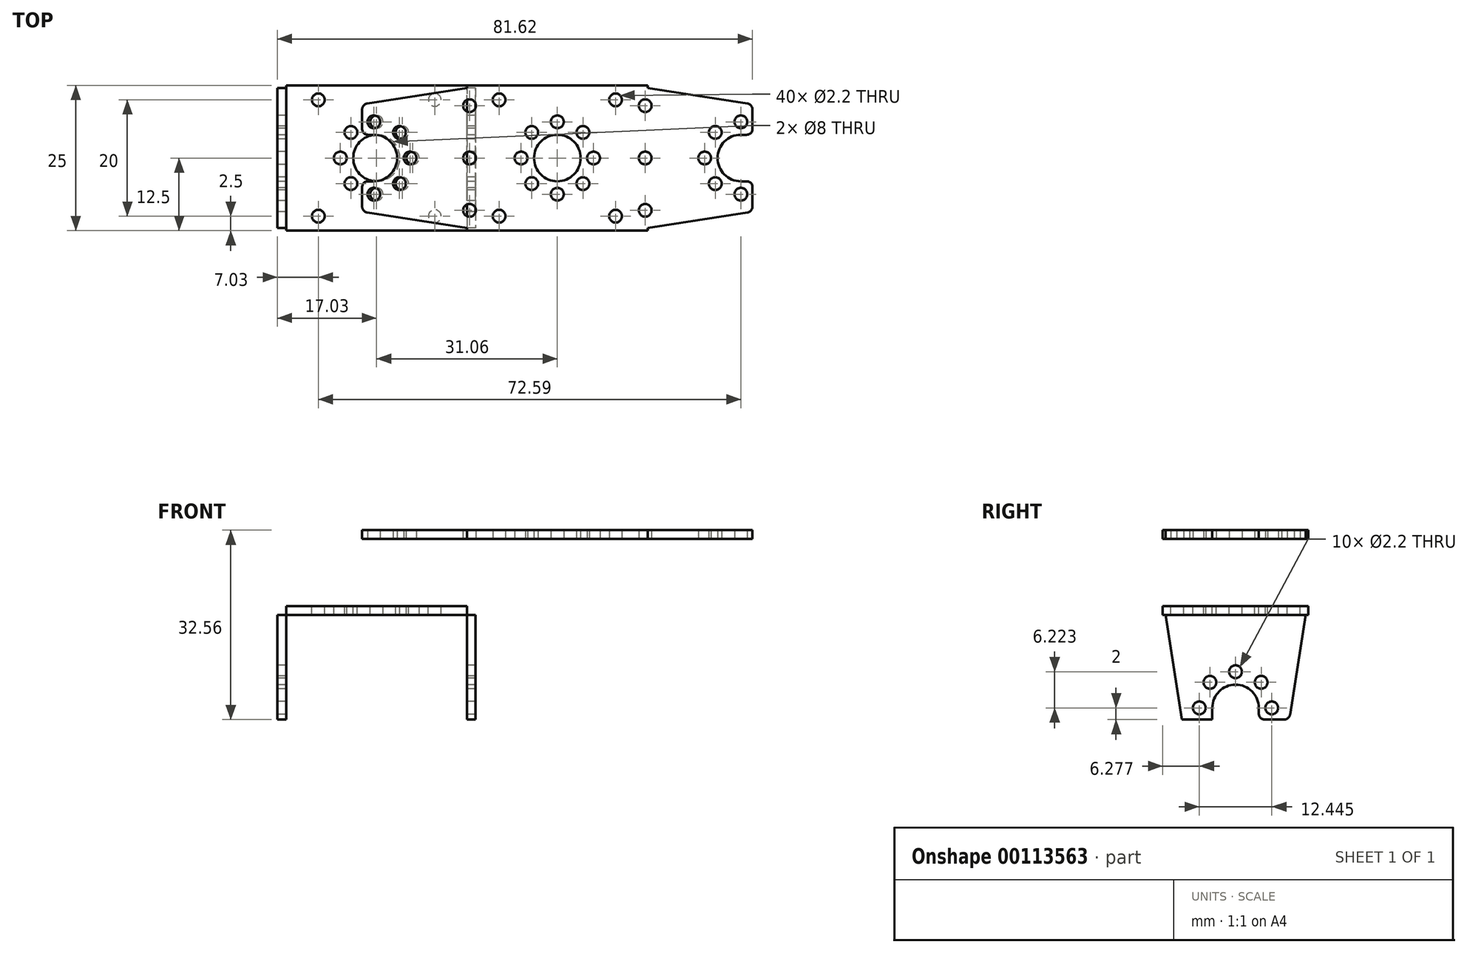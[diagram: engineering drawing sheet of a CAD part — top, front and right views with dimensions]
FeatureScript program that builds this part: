
annotation { "Feature Type Name" : "Feature", "Feature Type Description" : "" }
export const myFeature = defineFeature(function(context is Context, id is Id, definition is map)
    precondition{}
    {
        {
            var Q0;
            Q0=qCreatedBy(makeId("Front.planeOp"),FACE);
            var sketch = newSketch(context, id + "F0", { "sketchPlane" : qUnion([Q0])});
            skLineSegment(sketch, "E0.bottom", {"start": v(0, 0) * mm, "end": v(1.5, 0) * mm});
            skLineSegment(sketch, "E0.top", {"start": v(0, 19.5) * mm, "end": v(34.06, 19.5) * mm});
            skLineSegment(sketch, "E0.left", {"start": v(0, 0) * mm, "end": v(0, 19.5) * mm});
            skLineSegment(sketch, "E0.right", {"start": v(34.06, 0) * mm, "end": v(34.06, 19.5) * mm});
            skLineSegment(sketch, "E1.top", {"start": v(1.5, 18) * mm, "end": v(32.56, 18) * mm});
            skLineSegment(sketch, "E1.left", {"start": v(1.5, 0) * mm, "end": v(1.5, 18) * mm});
            skLineSegment(sketch, "E1.right", {"start": v(32.56, 0) * mm, "end": v(32.56, 18) * mm});
            skLineSegment(sketch, "E2.trimOffspring", {"start": v(32.56, 0) * mm, "end": v(34.06, 0) * mm});
            skSolve(sketch);
        }
        {
            var Q0;
            Q0=qSketchRegion(id+"F0",true);
            extrude(context, id + "F1", {"entities" : qUnion([Q0]), "depth" : 25 * mm});
        }
        {
            var Q0;
            Q0=makeQuery(id+"F1.opExtrude","SWEPT_FACE",FACE,{"disambiguationData":[OSD([sQuery(id+"F0.wireOp",EDGE,"E0.left")])]});
            var sketch = newSketch(context, id + "F2", { "sketchPlane" : qUnion([Q0])});
            skArc(sketch, "E3", {"start": v(16.5, 2) * mm, "mid": v(12.5, 6) * mm, "end": v(8.5, 2) * mm});
            skCircle(sketch, "E4", {"center": v(18.72, 2) * mm, "radius": 1.1 * mm});
            skCircle(sketch, "E5.1.0", {"center": v(16.9, 6.4) * mm, "radius": 1.1 * mm});
            skCircle(sketch, "E5.2.0", {"center": v(12.5, 8.22) * mm, "radius": 1.1 * mm});
            skCircle(sketch, "E5.3.0", {"center": v(8.1, 6.4) * mm, "radius": 1.1 * mm});
            skCircle(sketch, "E5.4.0", {"center": v(6.28, 2) * mm, "radius": 1.1 * mm});
            skLineSegment(sketch, "E6", {"start": v(8.5, 2) * mm, "end": v(8.5, 0) * mm});
            skLineSegment(sketch, "E7", {"start": v(16.5, 2) * mm, "end": v(16.5, 0) * mm});
            skLineSegment(sketch, "E8", {"start": v(8.5, 0) * mm, "end": v(16.5, 0) * mm});
            skLineSegment(sketch, "E9", {"start": v(12.5, 19.5) * mm, "end": v(12.5, 0) * mm, "construction": true});
            skPoint(sketch, "E10", {"position": v(12.5, 0) * mm});
            skLineSegment(sketch, "E11", {"start": v(3.28, 0) * mm, "end": v(0.47, 18) * mm});
            skLineSegment(sketch, "E12", {"start": v(3.28, 0) * mm, "end": v(0, 0) * mm});
            skLineSegment(sketch, "E13", {"start": v(0, 0) * mm, "end": v(0, 18) * mm});
            skLineSegment(sketch, "E14.MirrorCS", {"start": v(25, 0) * mm, "end": v(25, 18) * mm});
            skLineSegment(sketch, "E15.MirrorCS", {"start": v(21.72, 0) * mm, "end": v(24.53, 18) * mm});
            skLineSegment(sketch, "E16.MirrorCS", {"start": v(21.72, 0) * mm, "end": v(25, 0) * mm});
            skLineSegment(sketch, "E17", {"start": v(0, 18) * mm, "end": v(0.47, 18) * mm});
            skPoint(sketch, "E18.orphan", {"position": v(0, 21) * mm});
            skLineSegment(sketch, "E19.MirrorCS", {"start": v(25, 18) * mm, "end": v(24.53, 18) * mm});
            skPoint(sketch, "E20.orphan", {"position": v(25, 21) * mm});
            skSolve(sketch);
        }
        {
            var Q0;
            Q0=qSketchRegion(id+"F2",true);
            extrude(context, id + "F3", {"entities" : qUnion([Q0]), "operationType" : NewBodyOperationType.REMOVE, "endBound" : BoundingType.THROUGH_ALL, "oppositeDirection" : true, "depth" : 25 * mm});
        }
        {
            var Q0;
            Q0=makeQuery(id+"F1.opExtrude","SWEPT_FACE",FACE,{"disambiguationData":[OSD([sQuery(id+"F0.wireOp",EDGE,"E0.top")])]});
            var sketch = newSketch(context, id + "F4", { "sketchPlane" : qUnion([Q0])});
            skLineSegment(sketch, "E21", {"start": v(17.03, -1.64) * mm, "end": v(17.03, -24.77) * mm, "construction": true});
            skLineSegment(sketch, "E22", {"start": v(0, -12.5) * mm, "end": v(34.06, -12.5) * mm, "construction": true});
            skCircle(sketch, "E23", {"center": v(7.03, -2.5) * mm, "radius": 1.1 * mm});
            skCircle(sketch, "E24.MirrorC", {"center": v(27.03, -2.5) * mm, "radius": 1.1 * mm});
            skCircle(sketch, "E25.MirrorC", {"center": v(7.03, -22.5) * mm, "radius": 1.1 * mm});
            skCircle(sketch, "E26.MirrorC", {"center": v(27.03, -22.5) * mm, "radius": 1.1 * mm});
            skCircle(sketch, "E27", {"center": v(17.03, -12.5) * mm, "radius": 4 * mm});
            skLineSegment(sketch, "E28.bottom", {"start": v(21.43, -16.9) * mm, "end": v(12.63, -16.9) * mm, "construction": true});
            skLineSegment(sketch, "E28.top", {"start": v(21.43, -8.1) * mm, "end": v(12.63, -8.1) * mm, "construction": true});
            skLineSegment(sketch, "E28.left", {"start": v(21.43, -16.9) * mm, "end": v(21.43, -8.1) * mm, "construction": true});
            skLineSegment(sketch, "E28.right", {"start": v(12.63, -16.9) * mm, "end": v(12.63, -8.1) * mm, "construction": true});
            skCircle(sketch, "E29", {"center": v(12.63, -8.1) * mm, "radius": 1.1 * mm});
            skCircle(sketch, "E30.1.0", {"center": v(10.8, -12.5) * mm, "radius": 1.1 * mm});
            skCircle(sketch, "E30.2.0", {"center": v(12.63, -16.9) * mm, "radius": 1.1 * mm});
            skCircle(sketch, "E30.3.0", {"center": v(17.03, -18.72) * mm, "radius": 1.1 * mm});
            skCircle(sketch, "E31.1.4.0", {"center": v(21.43, -16.9) * mm, "radius": 1.1 * mm});
            skCircle(sketch, "E31.1.5.0", {"center": v(23.25, -12.5) * mm, "radius": 1.1 * mm});
            skCircle(sketch, "E31.1.6.0", {"center": v(21.43, -8.1) * mm, "radius": 1.1 * mm});
            skCircle(sketch, "E31.1.7.0", {"center": v(17.03, -6.28) * mm, "radius": 1.1 * mm});
            skPoint(sketch, "E32", {"position": v(17.03, -24.77) * mm});
            skPoint(sketch, "E33", {"position": v(17.03, 0) * mm});
            skPoint(sketch, "E34", {"position": v(17.03, -25) * mm});
            skSolve(sketch);
        }
        {
            var Q0;
            Q0=qSketchRegion(id+"F4",true);
            extrude(context, id + "F5", {"entities" : qUnion([Q0]), "operationType" : NewBodyOperationType.REMOVE, "endBound" : BoundingType.UP_TO_NEXT, "oppositeDirection" : true, "depth" : 25 * mm});
        }
        {
            var Q0;
            Q0=makeQuery(id+"F3.boolean.opBoolean","COPY",EDGE,{"disambiguationData":[OD(0.0)],"derivedFrom":makeQuery(id+"F3.opExtrude","SWEPT_EDGE",EDGE,{"disambiguationData":[OSD([sQuery(id+"F0.wireOp",EDGE,"E0.bottom"),sQuery(id+"F0.wireOp",EDGE,"E0.left"),sQuery(id+"F2.wireOp",EDGE,"E11"),sQuery(id+"F2.wireOp",EDGE,"E12")])]})});
            var Q1;
            Q1=makeQuery(id+"F3.boolean.opBoolean","COPY",EDGE,{"disambiguationData":[OD(0.0)],"derivedFrom":makeQuery(id+"F3.opExtrude","SWEPT_EDGE",EDGE,{"disambiguationData":[OSD([sQuery(id+"F0.wireOp",EDGE,"E0.bottom"),sQuery(id+"F0.wireOp",EDGE,"E0.left"),sQuery(id+"F2.wireOp",EDGE,"E6"),sQuery(id+"F2.wireOp",EDGE,"E8")])]})});
            var Q2;
            Q2=makeQuery(id+"F3.boolean.opBoolean","COPY",EDGE,{"disambiguationData":[OD(0.0)],"derivedFrom":makeQuery(id+"F3.opExtrude","SWEPT_EDGE",EDGE,{"disambiguationData":[OSD([sQuery(id+"F0.wireOp",EDGE,"E0.bottom"),sQuery(id+"F0.wireOp",EDGE,"E0.left"),sQuery(id+"F2.wireOp",EDGE,"E7"),sQuery(id+"F2.wireOp",EDGE,"E8")])]})});
            var Q3;
            Q3=makeQuery(id+"F3.boolean.opBoolean","COPY",EDGE,{"disambiguationData":[OD(0.0)],"derivedFrom":makeQuery(id+"F3.opExtrude","SWEPT_EDGE",EDGE,{"disambiguationData":[OSD([sQuery(id+"F0.wireOp",EDGE,"E0.bottom"),sQuery(id+"F0.wireOp",EDGE,"E0.left"),sQuery(id+"F2.wireOp",EDGE,"E15.MirrorCS"),sQuery(id+"F2.wireOp",EDGE,"E16.MirrorCS")])]})});
            var Q4;
            Q4=makeQuery(id+"F3.boolean.opBoolean","COPY",EDGE,{"disambiguationData":[OD(1.0)],"derivedFrom":makeQuery(id+"F3.opExtrude","SWEPT_EDGE",EDGE,{"disambiguationData":[OSD([sQuery(id+"F0.wireOp",EDGE,"E0.bottom"),sQuery(id+"F0.wireOp",EDGE,"E0.left"),sQuery(id+"F2.wireOp",EDGE,"E11"),sQuery(id+"F2.wireOp",EDGE,"E12")])]})});
            var Q5;
            Q5=makeQuery(id+"F3.boolean.opBoolean","COPY",EDGE,{"disambiguationData":[OD(1.0)],"derivedFrom":makeQuery(id+"F3.opExtrude","SWEPT_EDGE",EDGE,{"disambiguationData":[OSD([sQuery(id+"F0.wireOp",EDGE,"E0.bottom"),sQuery(id+"F0.wireOp",EDGE,"E0.left"),sQuery(id+"F2.wireOp",EDGE,"E6"),sQuery(id+"F2.wireOp",EDGE,"E8")])]})});
            var Q6;
            Q6=makeQuery(id+"F3.boolean.opBoolean","COPY",EDGE,{"disambiguationData":[OD(1.0)],"derivedFrom":makeQuery(id+"F3.opExtrude","SWEPT_EDGE",EDGE,{"disambiguationData":[OSD([sQuery(id+"F0.wireOp",EDGE,"E0.bottom"),sQuery(id+"F0.wireOp",EDGE,"E0.left"),sQuery(id+"F2.wireOp",EDGE,"E7"),sQuery(id+"F2.wireOp",EDGE,"E8")])]})});
            var Q7;
            Q7=makeQuery(id+"F3.boolean.opBoolean","COPY",EDGE,{"disambiguationData":[OD(1.0)],"derivedFrom":makeQuery(id+"F3.opExtrude","SWEPT_EDGE",EDGE,{"disambiguationData":[OSD([sQuery(id+"F0.wireOp",EDGE,"E0.bottom"),sQuery(id+"F0.wireOp",EDGE,"E0.left"),sQuery(id+"F2.wireOp",EDGE,"E15.MirrorCS"),sQuery(id+"F2.wireOp",EDGE,"E16.MirrorCS")])]})});
            fillet(context, id + "F6", {"entities" : qUnion([Q0, Q1, Q2, Q3, Q4, Q5, Q6, Q7]), "radius" : 1 * mm, "tangentPropagation" : true, "allowEdgeOverflow" : false});
        }
        {
            var Q0;
            Q0=makeQuery(id+"F1.opExtrude","CAP_FACE",FACE,{"disambiguationData":[OSD([sQuery(id+"F0.wireOp",EDGE,"E0.bottom"),sQuery(id+"F0.wireOp",EDGE,"E0.top"),sQuery(id+"F0.wireOp",EDGE,"E0.left"),sQuery(id+"F0.wireOp",EDGE,"E0.right"),sQuery(id+"F0.wireOp",EDGE,"E1.top"),sQuery(id+"F0.wireOp",EDGE,"E1.left"),sQuery(id+"F0.wireOp",EDGE,"E1.right"),sQuery(id+"F0.wireOp",EDGE,"E2.trimOffspring")])],"isStart":false});
            var sketch = newSketch(context, id + "F7", { "sketchPlane" : qUnion([Q0])});
            skLineSegment(sketch, "E35.bottom", {"start": v(0, 19.5) * mm, "end": v(1.5, 19.5) * mm});
            skLineSegment(sketch, "E35.top", {"start": v(0, 18) * mm, "end": v(1.5, 18) * mm});
            skLineSegment(sketch, "E35.left", {"start": v(0, 19.5) * mm, "end": v(0, 18) * mm});
            skLineSegment(sketch, "E35.right", {"start": v(1.5, 19.5) * mm, "end": v(1.5, 18) * mm});
            skLineSegment(sketch, "E36", {"start": v(17.03, 19.5) * mm, "end": v(17.03, 18) * mm, "construction": true});
            skLineSegment(sketch, "E37.MirrorCS", {"start": v(34.06, 19.5) * mm, "end": v(32.56, 19.5) * mm});
            skLineSegment(sketch, "E38.MirrorCS", {"start": v(32.56, 19.5) * mm, "end": v(32.56, 18) * mm});
            skLineSegment(sketch, "E39.MirrorCS", {"start": v(34.06, 19.5) * mm, "end": v(34.06, 18) * mm});
            skLineSegment(sketch, "E40.MirrorCS", {"start": v(34.06, 18) * mm, "end": v(32.56, 18) * mm});
            skSolve(sketch);
        }
        {
            var Q0;
            Q0 = qSketchRegion(id + "F7", true);
            extrude(context, id + "F8", {"entities" : qUnion([Q0]), "operationType" : NewBodyOperationType.REMOVE, "endBound" : BoundingType.THROUGH_ALL, "oppositeDirection" : true, "depth" : 25 * mm});
        }
        {
            var Q0;
            Q0=makeQuery(id+"F8.boolean.opBoolean","SPLIT",BODY,{"disambiguationData":[OD(0.0)],"derivedFrom":makeQuery(id+"F1.opExtrude","SWEPT_BODY",BODY,{"disambiguationData":[OSD([sQuery(id+"F0.wireOp",EDGE,"E0.bottom"),sQuery(id+"F0.wireOp",EDGE,"E0.top"),sQuery(id+"F0.wireOp",EDGE,"E0.left"),sQuery(id+"F0.wireOp",EDGE,"E0.right"),sQuery(id+"F0.wireOp",EDGE,"E1.top"),sQuery(id+"F0.wireOp",EDGE,"E1.left"),sQuery(id+"F0.wireOp",EDGE,"E1.right"),sQuery(id+"F0.wireOp",EDGE,"E2.trimOffspring")])]})});
            var Q1;
            {var subQ0=sQuery(id+"F0.wireOp",EDGE,"E1.top");Q1=makeQuery(id+"F8.boolean.opBoolean","MERGE",EDGE,{"disambiguationData":[OD(0.0)],"derivedFrom":[makeQuery(id+"F1.opExtrude","SWEPT_EDGE",EDGE,{"disambiguationData":[OSD([subQ0,sQuery(id+"F0.wireOp",EDGE,"E1.left")])]}),makeQuery(id+"F8.opExtrude","SWEPT_EDGE",EDGE,{"disambiguationData":[OSD([sQuery(id+"F0.wireOp",EDGE,"E0.left"),subQ0,sQuery(id+"F2.wireOp",EDGE,"E14.MirrorCS"),sQuery(id+"F2.wireOp",EDGE,"E19.MirrorCS"),sQuery(id+"F7.wireOp",EDGE,"E35.top"),sQuery(id+"F7.wireOp",EDGE,"E35.right")])]})]});}
            transform(context, id + "F9", {"entities" : qUnion([Q0]), "transformType" : TransformType.ROTATION, "transformAxis" : qUnion([Q1]), "angle" : 90 * degree, "makeCopy" : false});
        }
        {
            var Q0;
            Q0=makeQuery(id+"F8.boolean.opBoolean","SPLIT",BODY,{"disambiguationData":[OD(1.0)],"derivedFrom":makeQuery(id+"F1.opExtrude","SWEPT_BODY",BODY,{"disambiguationData":[OSD([sQuery(id+"F0.wireOp",EDGE,"E0.bottom"),sQuery(id+"F0.wireOp",EDGE,"E0.top"),sQuery(id+"F0.wireOp",EDGE,"E0.left"),sQuery(id+"F0.wireOp",EDGE,"E0.right"),sQuery(id+"F0.wireOp",EDGE,"E1.top"),sQuery(id+"F0.wireOp",EDGE,"E1.left"),sQuery(id+"F0.wireOp",EDGE,"E1.right"),sQuery(id+"F0.wireOp",EDGE,"E2.trimOffspring")])]})});
            var Q1;
            {var subQ0=sQuery(id+"F0.wireOp",EDGE,"E1.top");Q1=makeQuery(id+"F8.boolean.opBoolean","MERGE",EDGE,{"disambiguationData":[OD(0.0)],"derivedFrom":[makeQuery(id+"F1.opExtrude","SWEPT_EDGE",EDGE,{"disambiguationData":[OSD([subQ0,sQuery(id+"F0.wireOp",EDGE,"E1.right")])]}),makeQuery(id+"F8.opExtrude","SWEPT_EDGE",EDGE,{"disambiguationData":[OSD([sQuery(id+"F0.wireOp",EDGE,"E0.left"),subQ0,sQuery(id+"F2.wireOp",EDGE,"E14.MirrorCS"),sQuery(id+"F2.wireOp",EDGE,"E19.MirrorCS"),sQuery(id+"F7.wireOp",EDGE,"E38.MirrorCS"),sQuery(id+"F7.wireOp",EDGE,"E40.MirrorCS")])]})]});}
            transform(context, id + "F10", {"entities" : qUnion([Q0]), "transformType" : TransformType.ROTATION, "transformAxis" : qUnion([Q1]), "angle" : 270 * degree, "makeCopy" : false});
        }
        {
            var Q0;
            Q0=qCreatedBy(makeId("Top.planeOp"),FACE);
            var sketch = newSketch(context, id + "F11", { "sketchPlane" : qUnion([Q0])});
            skCircle(sketch, "E41.0", {"center": v(48.56, -6.28) * mm, "radius": 1.1 * mm});
            skCircle(sketch, "E42.0", {"center": v(44.16, -8.1) * mm, "radius": 1.1 * mm});
            skCircle(sketch, "E43.0", {"center": v(42.34, -12.5) * mm, "radius": 1.1 * mm});
            skCircle(sketch, "E44.0", {"center": v(44.16, -16.9) * mm, "radius": 1.1 * mm});
            skCircle(sketch, "E45.0", {"center": v(48.56, -18.72) * mm, "radius": 1.1 * mm});
            skCircle(sketch, "E46.0", {"center": v(23.25, -12.5) * mm, "radius": 1.1 * mm});
            skCircle(sketch, "E46.1", {"center": v(12.63, -8.1) * mm, "radius": 1.1 * mm});
            skCircle(sketch, "E46.2", {"center": v(10.8, -12.5) * mm, "radius": 1.1 * mm});
            skCircle(sketch, "E46.3", {"center": v(12.63, -16.9) * mm, "radius": 1.1 * mm});
            skCircle(sketch, "E46.4", {"center": v(17.03, -18.72) * mm, "radius": 1.1 * mm});
            skCircle(sketch, "E46.5", {"center": v(17.03, -12.5) * mm, "radius": 4 * mm});
            skCircle(sketch, "E46.6", {"center": v(21.43, -8.1) * mm, "radius": 1.1 * mm});
            skCircle(sketch, "E46.7", {"center": v(21.43, -16.9) * mm, "radius": 1.1 * mm});
            skCircle(sketch, "E46.8", {"center": v(17.03, -6.28) * mm, "radius": 1.1 * mm});
            skCircle(sketch, "E46.9", {"center": v(10.8, -12.5) * mm, "radius": 1.1 * mm});
            skCircle(sketch, "E46.10", {"center": v(17.03, -12.5) * mm, "radius": 4 * mm});
            skCircle(sketch, "E46.11", {"center": v(23.25, -12.5) * mm, "radius": 1.1 * mm});
            skCircle(sketch, "E46.12", {"center": v(21.43, -8.1) * mm, "radius": 1.1 * mm});
            skCircle(sketch, "E46.13", {"center": v(21.43, -16.9) * mm, "radius": 1.1 * mm});
            skCircle(sketch, "E46.14", {"center": v(17.03, -18.72) * mm, "radius": 1.1 * mm});
            skCircle(sketch, "E46.15", {"center": v(12.63, -16.9) * mm, "radius": 1.1 * mm});
            skCircle(sketch, "E46.16", {"center": v(12.63, -8.1) * mm, "radius": 1.1 * mm});
            skCircle(sketch, "E46.17", {"center": v(17.03, -6.28) * mm, "radius": 1.1 * mm});
            skArc(sketch, "E47.0", {"start": v(-15.5, -8.5) * mm, "mid": v(-16.2, -8.2) * mm, "end": v(-16.5, -7.5) * mm});
            skCircle(sketch, "E47.1", {"center": v(-14.5, -18.72) * mm, "radius": 1.1 * mm});
            skCircle(sketch, "E47.2", {"center": v(-8.28, -12.5) * mm, "radius": 1.1 * mm});
            skArc(sketch, "E47.3", {"start": v(-16.5, -17.5) * mm, "mid": v(-16.2, -16.8) * mm, "end": v(-15.5, -16.5) * mm});
            skArc(sketch, "E47.4", {"start": v(-14.5, -16.5) * mm, "mid": v(-10.5, -12.5) * mm, "end": v(-14.5, -8.5) * mm});
            skCircle(sketch, "E47.5", {"center": v(-10.1, -16.9) * mm, "radius": 1.1 * mm});
            skCircle(sketch, "E47.6", {"center": v(-14.5, -6.28) * mm, "radius": 1.1 * mm});
            skCircle(sketch, "E47.7", {"center": v(-10.1, -8.1) * mm, "radius": 1.1 * mm});
            skArc(sketch, "E47.8", {"start": v(-16.5, -7.5) * mm, "mid": v(-16.2, -8.2) * mm, "end": v(-15.5, -8.5) * mm});
            skLineSegment(sketch, "E47.9", {"start": v(-14.5, -8.5) * mm, "end": v(-15.5, -8.5) * mm});
            skArc(sketch, "E47.10", {"start": v(-14.5, -16.5) * mm, "mid": v(-10.5, -12.5) * mm, "end": v(-14.5, -8.5) * mm});
            skCircle(sketch, "E47.11", {"center": v(-10.1, -16.9) * mm, "radius": 1.1 * mm});
            skLineSegment(sketch, "E47.12", {"start": v(-14.5, -16.5) * mm, "end": v(-15.5, -16.5) * mm});
            skLineSegment(sketch, "E47.13", {"start": v(-16.5, -7.5) * mm, "end": v(-16.5, -4.13) * mm});
            skLineSegment(sketch, "E47.15", {"start": v(-14.5, -16.5) * mm, "end": v(-15.5, -16.5) * mm});
            skLineSegment(sketch, "E47.18", {"start": v(-16.5, -7.5) * mm, "end": v(-16.5, -4.13) * mm});
            skCircle(sketch, "E47.19", {"center": v(-14.5, -18.72) * mm, "radius": 1.1 * mm});
            skCircle(sketch, "E47.20", {"center": v(-8.28, -12.5) * mm, "radius": 1.1 * mm});
            skCircle(sketch, "E47.21", {"center": v(-10.1, -8.1) * mm, "radius": 1.1 * mm});
            skCircle(sketch, "E47.22", {"center": v(-14.5, -6.28) * mm, "radius": 1.1 * mm});
            skArc(sketch, "E47.25", {"start": v(-15.5, -16.5) * mm, "mid": v(-16.2, -16.8) * mm, "end": v(-16.5, -17.5) * mm});
            skLineSegment(sketch, "E47.26", {"start": v(-14.5, -8.5) * mm, "end": v(-15.5, -8.5) * mm});
            skLineSegment(sketch, "E48.0", {"start": v(-16.5, -20.87) * mm, "end": v(-16.5, -17.5) * mm});
            skArc(sketch, "E49.0", {"start": v(-15.65, -21.85) * mm, "mid": v(-16.26, -21.52) * mm, "end": v(-16.5, -20.87) * mm});
            skLineSegment(sketch, "E50.0", {"start": v(-15.65, -21.85) * mm, "end": v(1.5, -24.53) * mm});
            skLineSegment(sketch, "E51.0", {"start": v(-15.65, -3.15) * mm, "end": v(1.5, -0.47) * mm});
            skArc(sketch, "E52.0", {"start": v(-16.5, -4.13) * mm, "mid": v(-16.26, -3.48) * mm, "end": v(-15.65, -3.15) * mm});
            skCircle(sketch, "E53.0", {"center": v(7.03, -22.5) * mm, "radius": 1.1 * mm});
            skCircle(sketch, "E54.0", {"center": v(27.03, -22.5) * mm, "radius": 1.1 * mm});
            skCircle(sketch, "E55.0", {"center": v(27.03, -2.5) * mm, "radius": 1.1 * mm});
            skCircle(sketch, "E56.0", {"center": v(7.03, -2.5) * mm, "radius": 1.1 * mm});
            skLineSegment(sketch, "E57.0", {"start": v(1.5, 0) * mm, "end": v(32.56, 0) * mm});
            skLineSegment(sketch, "E58.0", {"start": v(1.5, -25) * mm, "end": v(32.56, -25) * mm});
            skLineSegment(sketch, "E59.0", {"start": v(49.71, -3.15) * mm, "end": v(32.56, -0.47) * mm});
            skLineSegment(sketch, "E60.0", {"start": v(49.71, -21.85) * mm, "end": v(32.56, -24.53) * mm});
            skArc(sketch, "E61.0", {"start": v(50.56, -20.87) * mm, "mid": v(50.32, -21.52) * mm, "end": v(49.71, -21.85) * mm});
            skLineSegment(sketch, "E62.0", {"start": v(50.56, -20.87) * mm, "end": v(50.56, -17.5) * mm});
            skArc(sketch, "E63.0", {"start": v(49.56, -16.5) * mm, "mid": v(50.27, -16.8) * mm, "end": v(50.56, -17.5) * mm});
            skArc(sketch, "E64.0", {"start": v(48.56, -16.5) * mm, "mid": v(44.56, -12.5) * mm, "end": v(48.56, -8.5) * mm});
            skLineSegment(sketch, "E65.0", {"start": v(48.56, -8.5) * mm, "end": v(49.56, -8.5) * mm});
            skArc(sketch, "E66.0", {"start": v(50.56, -7.5) * mm, "mid": v(50.27, -8.2) * mm, "end": v(49.56, -8.5) * mm});
            skLineSegment(sketch, "E67.0", {"start": v(50.56, -7.5) * mm, "end": v(50.56, -4.13) * mm});
            skArc(sketch, "E68.0", {"start": v(49.71, -3.15) * mm, "mid": v(50.32, -3.48) * mm, "end": v(50.56, -4.13) * mm});
            skLineSegment(sketch, "E69", {"start": v(32.56, 0) * mm, "end": v(32.56, -0.47) * mm});
            skLineSegment(sketch, "E70", {"start": v(32.56, -24.53) * mm, "end": v(32.56, -25) * mm});
            skLineSegment(sketch, "E71", {"start": v(1.5, -24.53) * mm, "end": v(1.5, -25) * mm});
            skLineSegment(sketch, "E72", {"start": v(1.5, 0) * mm, "end": v(1.5, -0.47) * mm});
            skLineSegment(sketch, "E73.0", {"start": v(48.56, -16.5) * mm, "end": v(49.56, -16.5) * mm});
            skSolve(sketch);
        }
        {
            var Q0;
            Q0 = qSketchRegion(id + "F11", true);
            extrude(context, id + "F12", {"entities" : qUnion([Q0]), "depth" : 1.5 * mm});
        }
        {
            var Q0;
            Q0=makeQuery(id+"F12.opExtrude","CAP_FACE",FACE,{"disambiguationData":[OSD([sQuery(id+"F11.wireOp",EDGE,"E41.0"),sQuery(id+"F11.wireOp",EDGE,"E42.0"),sQuery(id+"F11.wireOp",EDGE,"E43.0"),sQuery(id+"F11.wireOp",EDGE,"E44.0"),sQuery(id+"F11.wireOp",EDGE,"E45.0"),sQuery(id+"F11.wireOp",EDGE,"E46.9"),sQuery(id+"F11.wireOp",EDGE,"E46.10"),sQuery(id+"F11.wireOp",EDGE,"E46.11"),sQuery(id+"F11.wireOp",EDGE,"E46.12"),sQuery(id+"F11.wireOp",EDGE,"E46.13"),sQuery(id+"F11.wireOp",EDGE,"E46.14"),sQuery(id+"F11.wireOp",EDGE,"E46.15"),sQuery(id+"F11.wireOp",EDGE,"E46.16"),sQuery(id+"F11.wireOp",EDGE,"E46.17"),sQuery(id+"F11.wireOp",EDGE,"E47.8"),sQuery(id+"F11.wireOp",EDGE,"E47.10"),sQuery(id+"F11.wireOp",EDGE,"E47.11"),sQuery(id+"F11.wireOp",EDGE,"E47.15"),sQuery(id+"F11.wireOp",EDGE,"E47.18"),sQuery(id+"F11.wireOp",EDGE,"E47.19"),sQuery(id+"F11.wireOp",EDGE,"E47.20"),sQuery(id+"F11.wireOp",EDGE,"E47.21"),sQuery(id+"F11.wireOp",EDGE,"E47.22"),sQuery(id+"F11.wireOp",EDGE,"E47.25"),sQuery(id+"F11.wireOp",EDGE,"E47.26"),sQuery(id+"F11.wireOp",EDGE,"E48.0"),sQuery(id+"F11.wireOp",EDGE,"E49.0"),sQuery(id+"F11.wireOp",EDGE,"E50.0"),sQuery(id+"F11.wireOp",EDGE,"E51.0"),sQuery(id+"F11.wireOp",EDGE,"E52.0"),sQuery(id+"F11.wireOp",EDGE,"E53.0"),sQuery(id+"F11.wireOp",EDGE,"E54.0"),sQuery(id+"F11.wireOp",EDGE,"E55.0"),sQuery(id+"F11.wireOp",EDGE,"E56.0"),sQuery(id+"F11.wireOp",EDGE,"E57.0"),sQuery(id+"F11.wireOp",EDGE,"E58.0"),sQuery(id+"F11.wireOp",EDGE,"E59.0"),sQuery(id+"F11.wireOp",EDGE,"E60.0"),sQuery(id+"F11.wireOp",EDGE,"E61.0"),sQuery(id+"F11.wireOp",EDGE,"E62.0"),sQuery(id+"F11.wireOp",EDGE,"E63.0"),sQuery(id+"F11.wireOp",EDGE,"E64.0"),sQuery(id+"F11.wireOp",EDGE,"E65.0"),sQuery(id+"F11.wireOp",EDGE,"E66.0"),sQuery(id+"F11.wireOp",EDGE,"E67.0"),sQuery(id+"F11.wireOp",EDGE,"E68.0"),sQuery(id+"F11.wireOp",EDGE,"E69"),sQuery(id+"F11.wireOp",EDGE,"E70"),sQuery(id+"F11.wireOp",EDGE,"E71"),sQuery(id+"F11.wireOp",EDGE,"E72"),sQuery(id+"F11.wireOp",EDGE,"E73.0")])],"isStart":true});
            var sketch = newSketch(context, id + "F13", { "sketchPlane" : qUnion([Q0])});
            skLineSegment(sketch, "E74", {"start": v(17.03, 0) * mm, "end": v(17.03, 25) * mm, "construction": true});
            skLineSegment(sketch, "E75", {"start": v(1.94, 25) * mm, "end": v(1.94, 0) * mm, "construction": true});
            skLineSegment(sketch, "E76", {"start": v(1.94, 12.5) * mm, "end": v(17.03, 12.5) * mm, "construction": true});
            skCircle(sketch, "E77", {"center": v(1.94, 21.5) * mm, "radius": 1.1 * mm});
            skCircle(sketch, "E78", {"center": v(1.94, 12.5) * mm, "radius": 1.1 * mm});
            skCircle(sketch, "E79.MirrorC", {"center": v(1.94, 3.5) * mm, "radius": 1.1 * mm});
            skCircle(sketch, "E80.MirrorC", {"center": v(32.12, 12.5) * mm, "radius": 1.1 * mm});
            skCircle(sketch, "E81.MirrorC", {"center": v(32.12, 3.5) * mm, "radius": 1.1 * mm});
            skCircle(sketch, "E82.MirrorC", {"center": v(32.12, 21.5) * mm, "radius": 1.1 * mm});
            skSolve(sketch);
        }
        {
            var Q0;
            Q0 = qSketchRegion(id + "F13", true);
            extrude(context, id + "F14", {"entities" : qUnion([Q0]), "operationType" : NewBodyOperationType.REMOVE, "endBound" : BoundingType.UP_TO_NEXT, "oppositeDirection" : true, "depth" : 25 * mm});
        }
    });
